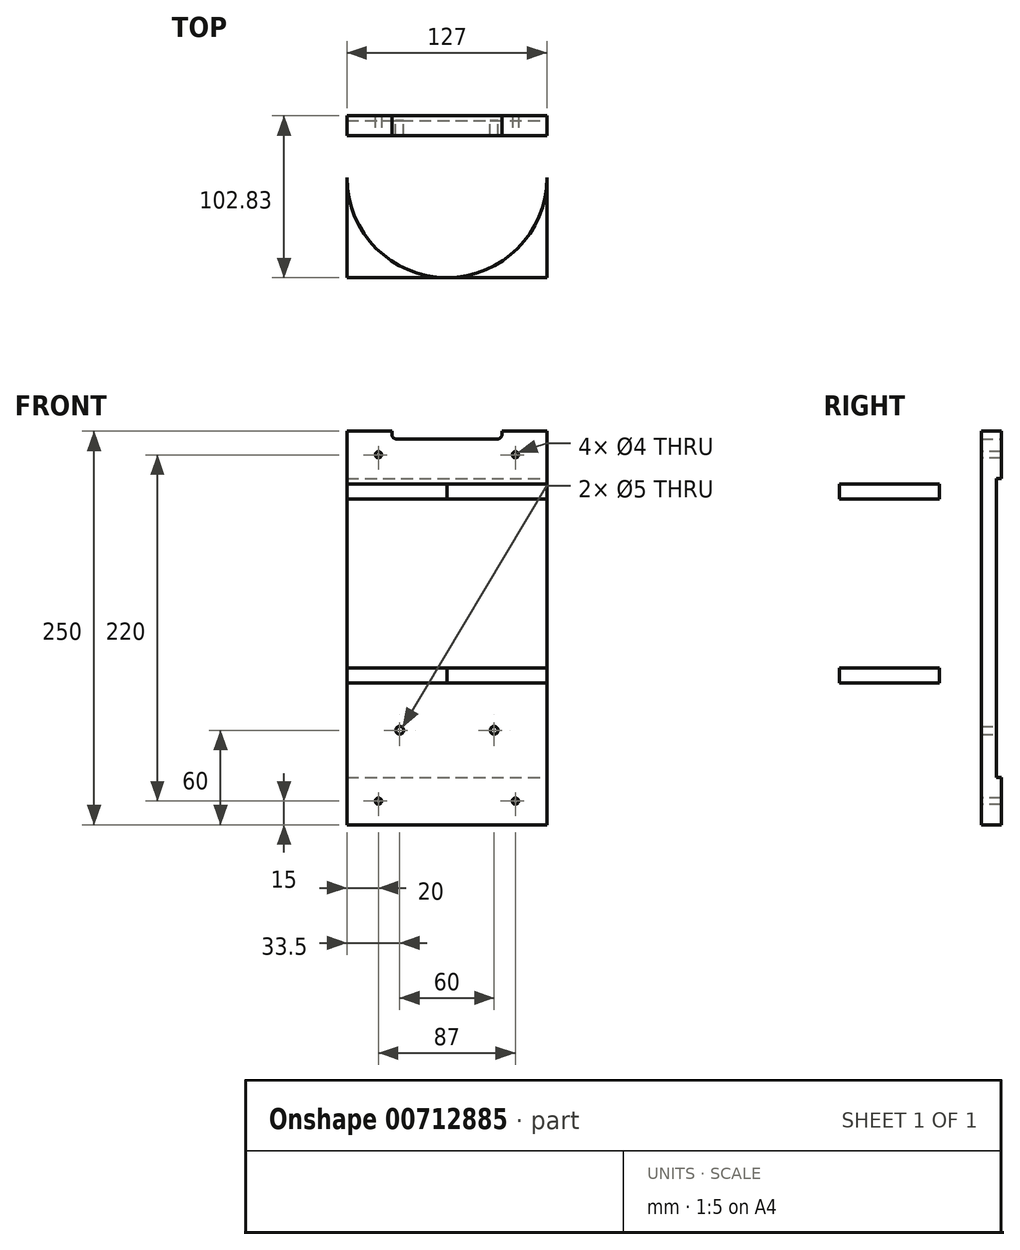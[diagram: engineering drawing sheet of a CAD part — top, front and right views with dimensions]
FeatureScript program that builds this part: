
annotation { "Feature Type Name" : "Feature", "Feature Type Description" : "" }
export const myFeature = defineFeature(function(context is Context, id is Id, definition is map)
    precondition{}
    {
        {
            var Q0;
            Q0=qCreatedBy(makeId("Front.planeOp"),FACE);
            var sketch = newSketch(context, id + "F0", { "sketchPlane" : qUnion([Q0])});
            skLineSegment(sketch, "E0.top", {"start": v(63.5, -125) * mm, "end": v(-63.5, -125) * mm});
            skLineSegment(sketch, "E0.left", {"start": v(63.5, 125) * mm, "end": v(63.5, -125) * mm});
            skLineSegment(sketch, "E0.right", {"start": v(-63.5, 125) * mm, "end": v(-63.5, -125) * mm});
            skPoint(sketch, "E0.middle", {"position": v(0, 0) * mm});
            skLineSegment(sketch, "E1", {"start": v(-63.5, 95) * mm, "end": v(63.5, 95) * mm});
            skLineSegment(sketch, "E2", {"start": v(-63.5, -95) * mm, "end": v(63.5, -95) * mm});
            skLineSegment(sketch, "E3", {"start": v(-63.5, -35) * mm, "end": v(63.5, -35) * mm, "construction": true});
            skLineSegment(sketch, "E4", {"start": v(63.5, -25.47) * mm, "end": v(-63.5, -25.47) * mm, "construction": true});
            skLineSegment(sketch, "E5", {"start": v(63.5, 81.99) * mm, "end": v(-63.5, 81.99) * mm, "construction": true});
            skLineSegment(sketch, "E6", {"start": v(-63.5, 91.52) * mm, "end": v(63.5, 91.52) * mm, "construction": true});
            skLineSegment(sketch, "E7.top", {"start": v(35, 120) * mm, "end": v(-35, 120) * mm});
            skLineSegment(sketch, "E7.left", {"start": v(35, 125) * mm, "end": v(35, 120) * mm});
            skLineSegment(sketch, "E7.right", {"start": v(-35, 125) * mm, "end": v(-35, 120) * mm});
            skPoint(sketch, "E7.middle", {"position": v(0, 122.5) * mm});
            skLineSegment(sketch, "E8", {"start": v(-63.5, 125) * mm, "end": v(-35, 125) * mm});
            skLineSegment(sketch, "E9", {"start": v(35, 125) * mm, "end": v(63.5, 125) * mm});
            skLineSegment(sketch, "E10", {"start": v(-30, -65) * mm, "end": v(30, -65) * mm, "construction": true});
            skPoint(sketch, "E11", {"position": v(0, -65) * mm});
            skPoint(sketch, "E12", {"position": v(-30, -65) * mm});
            skPoint(sketch, "E13", {"position": v(30, -65) * mm});
            skLineSegment(sketch, "E14.bottom", {"start": v(43.5, 110) * mm, "end": v(-43.5, 110) * mm, "construction": true});
            skLineSegment(sketch, "E14.top", {"start": v(43.5, -110) * mm, "end": v(-43.5, -110) * mm, "construction": true});
            skLineSegment(sketch, "E14.left", {"start": v(43.5, 110) * mm, "end": v(43.5, -110) * mm, "construction": true});
            skLineSegment(sketch, "E14.right", {"start": v(-43.5, 110) * mm, "end": v(-43.5, -110) * mm, "construction": true});
            skPoint(sketch, "E15", {"position": v(-43.5, 110) * mm});
            skPoint(sketch, "E16", {"position": v(43.5, 110) * mm});
            skPoint(sketch, "E17", {"position": v(-43.5, -110) * mm});
            skPoint(sketch, "E18", {"position": v(43.5, -110) * mm});
            skSolve(sketch);
        }
        {
            var Q0;
            Q0 = qSketchRegion(id + "F0", true);
            extrude(context, id + "F1", {"entities" : qUnion([Q0]), "depth" : 9.53 * mm, "offsetDistance" : 25 * mm});
        }
        {
            var Q0;
            {var subQ0=sQuery(id+"F0.wireOp",EDGE,"E1");Q0=makeQuery(id+"F0.imprint","IMPRINT",FACE,{"disambiguationData":[TD([[makeQuery(id+"F0.imprint","IMPRINT",EDGE,{"derivedFrom":subQ0}),1.0]])]});}
            var Q1;
            {var subQ0=sQuery(id+"F0.wireOp",EDGE,"E0.top");Q1=makeQuery(id+"F0.imprint","IMPRINT",FACE,{"disambiguationData":[TD([[makeQuery(id+"F0.imprint","IMPRINT",EDGE,{"derivedFrom":subQ0}),-1.0]])]});}
            extrude(context, id + "F2", {"entities" : qUnion([Q0, Q1]), "operationType" : NewBodyOperationType.ADD, "oppositeDirection" : true, "depth" : 3.18 * mm, "offsetDistance" : 25 * mm});
        }
        {
            var Q0;
            Q0=makeQuery(id+"F1.opExtrude","CAP_FACE",FACE,{"disambiguationData":[OSD([sQuery(id+"F0.wireOp",EDGE,"E0.top"),sQuery(id+"F0.wireOp",EDGE,"E0.left"),sQuery(id+"F0.wireOp",EDGE,"E0.right"),sQuery(id+"F0.wireOp",EDGE,"E7.top"),sQuery(id+"F0.wireOp",EDGE,"E7.left"),sQuery(id+"F0.wireOp",EDGE,"E7.right"),sQuery(id+"F0.wireOp",EDGE,"E8"),sQuery(id+"F0.wireOp",EDGE,"E9")])],"isStart":false});
            var sketch = newSketch(context, id + "F3", { "sketchPlane" : qUnion([Q0])});
            skPoint(sketch, "E19.0", {"position": v(-43.5, 110) * mm});
            skPoint(sketch, "E19.1", {"position": v(43.5, 110) * mm});
            skPoint(sketch, "E19.2", {"position": v(43.5, -110) * mm});
            skPoint(sketch, "E19.3", {"position": v(-43.5, -110) * mm});
            skPoint(sketch, "E19.4", {"position": v(-30, -65) * mm});
            skPoint(sketch, "E19.5", {"position": v(30, -65) * mm});
            skLineSegment(sketch, "E20.0", {"start": v(-63.5, 91.52) * mm, "end": v(63.5, 91.52) * mm});
            skLineSegment(sketch, "E20.1", {"start": v(63.5, 81.99) * mm, "end": v(-63.5, 81.99) * mm});
            skLineSegment(sketch, "E20.2", {"start": v(63.5, -25.47) * mm, "end": v(-63.5, -25.47) * mm});
            skLineSegment(sketch, "E20.3", {"start": v(-63.5, -35) * mm, "end": v(63.5, -35) * mm});
            skLineSegment(sketch, "E21", {"start": v(-63.5, -35) * mm, "end": v(-63.5, -25.47) * mm});
            skLineSegment(sketch, "E22", {"start": v(-63.5, 81.99) * mm, "end": v(-63.5, 91.52) * mm});
            skLineSegment(sketch, "E23", {"start": v(63.5, 91.52) * mm, "end": v(63.5, 81.99) * mm});
            skLineSegment(sketch, "E24", {"start": v(63.5, -25.47) * mm, "end": v(63.5, -35) * mm});
            skSolve(sketch);
        }
        {
            var Q0;
            Q0=sQuery(id+"F3.wireOp",VERTEX,"E19.0");
            var Q1;
            Q1=sQuery(id+"F3.wireOp",VERTEX,"E19.1");
            var Q2;
            Q2=sQuery(id+"F3.wireOp",VERTEX,"E19.3");
            var Q3;
            Q3=sQuery(id+"F3.wireOp",VERTEX,"E19.2");
            var Q4;
            Q4=makeQuery(id+"F1.opExtrude","SWEPT_BODY",BODY,{"disambiguationData":[OSD([sQuery(id+"F0.wireOp",EDGE,"E0.top"),sQuery(id+"F0.wireOp",EDGE,"E0.left"),sQuery(id+"F0.wireOp",EDGE,"E0.right"),sQuery(id+"F0.wireOp",EDGE,"E7.top"),sQuery(id+"F0.wireOp",EDGE,"E7.left"),sQuery(id+"F0.wireOp",EDGE,"E7.right"),sQuery(id+"F0.wireOp",EDGE,"E8"),sQuery(id+"F0.wireOp",EDGE,"E9")])]});
            hole(context, id + "F4", {"style" : HoleStyle.SIMPLE, "endStyle" : HoleEndStyle.THROUGH, "holeDiameter" : 4 * mm, "majorDiameter" : 5 * mm, "isTappedThrough" : true, "tappedDepth" : 12 * mm, "tapClearance" : 3, "startFromSketch" : true, "locations" : qUnion([Q0, Q1, Q2, Q3]), "scope" : qUnion([Q4])});
        }
        {
            var Q0;
            Q0=sQuery(id+"F0.wireOp",VERTEX,"E12");
            var Q1;
            Q1=sQuery(id+"F0.wireOp",VERTEX,"E13");
            var Q2;
            Q2=makeQuery(id+"F1.opExtrude","SWEPT_BODY",BODY,{"disambiguationData":[OSD([sQuery(id+"F0.wireOp",EDGE,"E0.top"),sQuery(id+"F0.wireOp",EDGE,"E0.left"),sQuery(id+"F0.wireOp",EDGE,"E0.right"),sQuery(id+"F0.wireOp",EDGE,"E7.top"),sQuery(id+"F0.wireOp",EDGE,"E7.left"),sQuery(id+"F0.wireOp",EDGE,"E7.right"),sQuery(id+"F0.wireOp",EDGE,"E8"),sQuery(id+"F0.wireOp",EDGE,"E9")])]});
            hole(context, id + "F5", {"style" : HoleStyle.SIMPLE, "endStyle" : HoleEndStyle.THROUGH, "oppositeDirection" : true, "holeDiameter" : 5 * mm, "majorDiameter" : 5 * mm, "isTappedThrough" : true, "tappedDepth" : 12 * mm, "tapClearance" : 3, "startFromSketch" : true, "locations" : qUnion([Q0, Q1]), "scope" : qUnion([Q2])});
        }
        {
            var Q0;
            Q0 = qSketchRegion(id + "F3", true);
            extrude(context, id + "F6", {"entities" : qUnion([Q0]), "operationType" : NewBodyOperationType.ADD, "depth" : 90.12 * mm, "offsetDistance" : 25 * mm});
        }
        {
            var Q0;
            Q0=makeQuery(id+"F6.opExtrude","SWEPT_FACE",FACE,{"disambiguationData":[OSD([sQuery(id+"F3.wireOp",EDGE,"E20.0")])]});
            var sketch = newSketch(context, id + "F7", { "sketchPlane" : qUnion([Q0])});
            skCircle(sketch, "E25", {"center": v(0, -57.03) * mm, "radius": 32.5 * mm});
            skArc(sketch, "E26", {"start": v(63.5, -36.15) * mm, "mid": v(0, -99.65) * mm, "end": v(-63.5, -36.15) * mm});
            skPoint(sketch, "E26.centerSnap0", {"position": v(0, -9.53) * mm});
            skPoint(sketch, "E27", {"position": v(45, -63.53) * mm});
            skLineSegment(sketch, "E28", {"start": v(-48.6, -77.03) * mm, "end": v(48.6, -77.03) * mm, "construction": true});
            skLineSegment(sketch, "E29", {"start": v(-38, -87.02) * mm, "end": v(-38, -77.03) * mm});
            skLineSegment(sketch, "E30", {"start": v(-38, -77.03) * mm, "end": v(-48.6, -77.03) * mm});
            skLineSegment(sketch, "E31", {"start": v(38, -87.02) * mm, "end": v(38, -77.03) * mm});
            skLineSegment(sketch, "E32", {"start": v(38, -77.03) * mm, "end": v(48.6, -77.03) * mm});
            skLineSegment(sketch, "E33", {"start": v(-54.32, -69.03) * mm, "end": v(-30.2, -69.03) * mm});
            skLineSegment(sketch, "E34", {"start": v(-30.2, -69.03) * mm, "end": v(-30.92, -67.03) * mm});
            skLineSegment(sketch, "E35", {"start": v(-30.92, -67.03) * mm, "end": v(-55.49, -67.03) * mm});
            skSolve(sketch);
        }
        {
            var Q0;
            Q0=makeQuery(id+"F7.imprint","IMPRINT",FACE,{"disambiguationData":[TD([[makeQuery(id+"F7.imprint","IMPRINT",EDGE,{"derivedFrom":sQuery(id+"F7.wireOp",EDGE,"E25")}),1.0]])]});
            var Q1;
            {var subQ0=sQuery(id+"F7.wireOp",EDGE,"E26");var subQ1=sQuery(id+"F3.wireOp",EDGE,"E20.0");var subQ4=makeQuery(id+"F6.opExtrude","CAP_EDGE",EDGE,{"disambiguationData":[OSD([subQ1])],"isStart":false});var subQ5=makeQuery(id+"F7.imprint","INTERSECT",VERTEX,{"derivedFrom":[subQ4,subQ0]});Q1=makeQuery(id+"F7.imprint","IMPRINT",FACE,{"disambiguationData":[TD([[makeQuery(id+"F7.imprint","IMPRINT",EDGE,{"disambiguationData":[TD([[subQ5,-1.0]])],"derivedFrom":subQ0}),1.0]])]});}
            var Q2;
            {var subQ0=sQuery(id+"F7.wireOp",EDGE,"E26");var subQ1=sQuery(id+"F3.wireOp",EDGE,"E20.0");var subQ4=makeQuery(id+"F6.opExtrude","CAP_EDGE",EDGE,{"disambiguationData":[OSD([subQ1])],"isStart":false});var subQ5=makeQuery(id+"F7.imprint","INTERSECT",VERTEX,{"derivedFrom":[subQ4,subQ0]});Q2=makeQuery(id+"F7.imprint","IMPRINT",FACE,{"disambiguationData":[TD([[makeQuery(id+"F7.imprint","IMPRINT",EDGE,{"disambiguationData":[TD([[subQ5,1.0]])],"derivedFrom":subQ0}),1.0]])]});}
            var Q3;
            {var subQ0=sQuery(id+"F7.wireOp",EDGE,"E29");Q3=makeQuery(id+"F7.imprint","IMPRINT",FACE,{"disambiguationData":[TD([[makeQuery(id+"F7.imprint","IMPRINT",EDGE,{"derivedFrom":subQ0}),1.0]])]});}
            var Q4;
            {var subQ0=sQuery(id+"F7.wireOp",EDGE,"E31");Q4=makeQuery(id+"F7.imprint","IMPRINT",FACE,{"disambiguationData":[TD([[makeQuery(id+"F7.imprint","IMPRINT",EDGE,{"derivedFrom":subQ0}),-1.0]])]});}
            var Q5;
            {var subQ1=sQuery(id+"F7.wireOp",EDGE,"E33");Q5=makeQuery(id+"F7.imprint","IMPRINT",FACE,{"disambiguationData":[TD([[makeQuery(id+"F7.imprint","IMPRINT",EDGE,{"derivedFrom":subQ1}),1.0]])]});}
            extrude(context, id + "F8", {"entities" : qUnion([Q0, Q1, Q2, Q3, Q4, Q5]), "operationType" : NewBodyOperationType.REMOVE, "endBound" : BoundingType.THROUGH_ALL, "oppositeDirection" : true, "depth" : 25 * mm, "offsetDistance" : 25 * mm});
        }
        {
            var Q0;
            Q0=sQuery(id+"F7.wireOp",VERTEX,"E27");
            var Q1;
            Q1=makeQuery(id+"F1.opExtrude","SWEPT_BODY",BODY,{"disambiguationData":[OSD([sQuery(id+"F0.wireOp",EDGE,"E0.top"),sQuery(id+"F0.wireOp",EDGE,"E0.left"),sQuery(id+"F0.wireOp",EDGE,"E0.right"),sQuery(id+"F0.wireOp",EDGE,"E7.top"),sQuery(id+"F0.wireOp",EDGE,"E7.left"),sQuery(id+"F0.wireOp",EDGE,"E7.right"),sQuery(id+"F0.wireOp",EDGE,"E8"),sQuery(id+"F0.wireOp",EDGE,"E9")])]});
            hole(context, id + "F9", {"style" : HoleStyle.SIMPLE, "endStyle" : HoleEndStyle.THROUGH, "holeDiameter" : 12 * mm, "majorDiameter" : 5 * mm, "isTappedThrough" : true, "tappedDepth" : 12 * mm, "tapClearance" : 3, "startFromSketch" : true, "locations" : qUnion([Q0]), "scope" : qUnion([Q1])});
        }
        {
            var Q0;
            {var subQ0=sQuery(id+"F7.wireOp",EDGE,"E30");var subQ1=sQuery(id+"F7.wireOp",EDGE,"E29");Q0=makeQuery(id+"F8.boolean.opBoolean","COPY",EDGE,{"disambiguationData":[TD([makeQuery(id+"F6.opExtrude","SWEPT_FACE",FACE,{"disambiguationData":[OSD([sQuery(id+"F3.wireOp",EDGE,"E20.0")])]})])],"derivedFrom":makeQuery(id+"F8.opExtrude","SWEPT_EDGE",EDGE,{"disambiguationData":[OSD([subQ1,subQ0])]})});}
            var Q1;
            {var subQ0=sQuery(id+"F7.wireOp",EDGE,"E29");var subQ1=sQuery(id+"F7.wireOp",EDGE,"E30");Q1=makeQuery(id+"F8.boolean.opBoolean","COPY",EDGE,{"disambiguationData":[TD([makeQuery(id+"F6.opExtrude","SWEPT_FACE",FACE,{"disambiguationData":[OSD([sQuery(id+"F3.wireOp",EDGE,"E20.2")])]})])],"derivedFrom":makeQuery(id+"F8.opExtrude","SWEPT_EDGE",EDGE,{"disambiguationData":[OSD([subQ0,subQ1])]})});}
            var Q2;
            {var subQ0=sQuery(id+"F7.wireOp",EDGE,"E32");var subQ1=sQuery(id+"F7.wireOp",EDGE,"E31");Q2=makeQuery(id+"F8.boolean.opBoolean","COPY",EDGE,{"disambiguationData":[TD([makeQuery(id+"F6.opExtrude","SWEPT_FACE",FACE,{"disambiguationData":[OSD([sQuery(id+"F3.wireOp",EDGE,"E20.2")])]})])],"derivedFrom":makeQuery(id+"F8.opExtrude","SWEPT_EDGE",EDGE,{"disambiguationData":[OSD([subQ1,subQ0])]})});}
            var Q3;
            {var subQ0=sQuery(id+"F7.wireOp",EDGE,"E31");var subQ1=sQuery(id+"F7.wireOp",EDGE,"E32");Q3=makeQuery(id+"F8.boolean.opBoolean","COPY",EDGE,{"disambiguationData":[TD([makeQuery(id+"F6.opExtrude","SWEPT_FACE",FACE,{"disambiguationData":[OSD([sQuery(id+"F3.wireOp",EDGE,"E20.0")])]})])],"derivedFrom":makeQuery(id+"F8.opExtrude","SWEPT_EDGE",EDGE,{"disambiguationData":[OSD([subQ0,subQ1])]})});}
            var Q4;
            {var subQ0=sQuery(id+"F0.wireOp",EDGE,"E7.right");var subQ1=sQuery(id+"F0.wireOp",EDGE,"E7.top");Q4=makeQuery(id+"F2.boolean.opBoolean","MERGE",EDGE,{"derivedFrom":[makeQuery(id+"F1.opExtrude","SWEPT_EDGE",EDGE,{"disambiguationData":[OSD([subQ1,subQ0])]}),makeQuery(id+"F2.opExtrude","SWEPT_EDGE",EDGE,{"disambiguationData":[OSD([subQ1,subQ0])]})]});}
            var Q5;
            {var subQ0=sQuery(id+"F0.wireOp",EDGE,"E7.left");var subQ1=sQuery(id+"F0.wireOp",EDGE,"E7.top");Q5=makeQuery(id+"F2.boolean.opBoolean","MERGE",EDGE,{"derivedFrom":[makeQuery(id+"F1.opExtrude","SWEPT_EDGE",EDGE,{"disambiguationData":[OSD([subQ1,subQ0])]}),makeQuery(id+"F2.opExtrude","SWEPT_EDGE",EDGE,{"disambiguationData":[OSD([subQ1,subQ0])]})]});}
            fillet(context, id + "F10", {"entities" : qUnion([Q0, Q1, Q2, Q3, Q4, Q5]), "radius" : 3.17 * mm, "tangentPropagation" : true, "allowEdgeOverflow" : false});
        }
    });
